# Revit family: P350205-009
name_source: partatom
category: Lighting Fixtures
units: mm (PartAtom-declared; Revit-internal decimal feet)

## family parameters
Cut with Voids When Loaded = No
Host = Face
Light Source = No
OmniClass Number = 23.80.70.11.14.17
OmniClass Title = Direct/Indirect
Part Type = Normal
Room Calculation Point = No
Round Connector Dimension = Use Diameter
Shared = Yes

## types (1)
- P350205-009
    Apparent Load = 60 VA
    Assembly Code = D5020200
    Connector Description = Lighting Connector
    Default Elevation = 48 "
    Description = Rushton Collection Two-Light Brushed Nickel and Clear Glass Industrial Style Flush Mount Ceiling Light
    Features = Application: Integrate historical industrial elegance into your home decor with the Rushton Collection 2-Light Brushed Nickel Clear Glass Industrial Flush Mount Ceiling Light is ideal for any hallway, stairwell, entryway, kitchen, bathroom, or sitting room.
Styles: Perfect for farmhouse and urban industrial style settings.
Finish: The circular ceiling plate, smooth light bases, and decorative detail at the bottom of the shade are coated in a beautiful brushed nickel finish.
Materials: Constructed from steel to ensure a long product lifespan.
Glass/Shade: Light sources glow from within the clear glass shade for elegant illumination.
Bulbs: For ideal illumination, use 2 medium base bulbs that are sold separately (60w max - LED/CFL/incandescent). Compatible with dimmable bulbs.
Dimensions: Measures 12-inch diameter by 6-7/8-inch height.
Certifications: cCSAus damp location listed.
Pairs with: Pairs with Hemsworth and Lockhart collections from Progress Lighting.
Warranty: Our 1-Year Limited Warranty guarantees your complete satisfaction with your purchase and includes professional after-sales customer service support.
    Fixture distribution = Direct
    Glass = Paint - Hubbell - White Texture
    Gold = Hubbell - Gold
    Housing Material = Hubbell Metal Nickel
    Lamp = LED/CFL/incandescent
    Load Classification = Lighting
    Manufacturer = Progress Lighting
    Model = P350205-009
    Power Factor = 1
    Product Documentation Link = https://hubbellcdn.com
    Product Link = https://www.hubbell.com
    URL = https://www.hubbell.com
    Voltage = 120 V
    Warranty = 1 year Warranty
    Wattage Comments = 60W
    Watts = 60 W
    Widh = 12 "

## geometry (parser evidence)
native form markers: Sweep x5
no freeform markers — native parametric forms only
